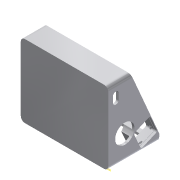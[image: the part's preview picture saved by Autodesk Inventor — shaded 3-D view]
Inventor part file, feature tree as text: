
AUTODESK INVENTOR PART (.ipt)
format: ipt  version: 2019.4 (Build 234330000, 330)  size: 572,928 bytes
history: native  units: mm
features: extrude x14, sketch x14, reference x13, projected_geometry x11, other x7, plane x2, chamfer x1
ambient origin geometry x8: Origin, YZ Plane, XZ Plane, XY Plane, X Axis, Y Axis, Z Axis, Center Point
bodies: Solid1 (feature_tree)
feature tree (62):
  plane  "Work Plane1"
  extrude  "Extrusion1"  Depth=5.0mm
  sketch  "Sketch2"  dims[d3=90.0mm d4=3.0mm d5=0.0mm]
  plane  "Work Plane2"
  extrude  "Extrusion2"  Depth=3.0mm TaperAngle=0.0deg
  extrude  "Extrusion3"  Depth=3.0mm
  extrude  "Extrusion4"  Depth=3.0mm TaperAngle=0.0deg
  extrude  "Extrusion5"  Depth=3.0mm TaperAngle=0.0deg
  extrude  "Extrusion6"  Depth=3.0mm TaperAngle=0.0deg
  extrude  "Extrusion7"  TaperAngle=0.0deg  [1 undecoded]
  extrude  "Extrusion8"  Depth=10.0mm TaperAngle=0.0deg
  extrude  "Extrusion9"  Depth=2.9mm
  extrude  "Extrusion10"  Depth=2.9mm
  extrude  "Extrusion11"  Depth=20.0mm TaperAngle=0.0deg
  extrude  "Extrusion12"  Depth=20.0mm TaperAngle=0.0deg
  extrude  "Extrusion13"  TaperAngle=90.0deg  [1 undecoded]
  extrude  "Extrusion14"  TaperAngle=180.0deg  [1 undecoded]
  chamfer  "Chamfer1"  Distance=11.0mm
  sketch  "Sketch1"  dims[d1=5.0mm d2=5.0mm]
  reference  "Reference1"
  reference  "Reference2"
  projected_geometry  "Projected Loop1"
  sketch  "Sketch3"  dims[d6=5.0mm d7=3.0mm]
  projected_geometry  "Projected Loop2"
  sketch  "Sketch4"  dims[d8=3.0mm d9=0.0mm d10=3.0mm d11=0.0mm]
  reference  "Reference3"
  sketch  "Sketch5"  dims[d12=3.0mm d13=0.0mm d14=3.0mm d15=0.0mm]
  reference  "Reference4"
  reference  "Reference5"
  reference  "Reference6"
  reference  "Reference7"
  reference  "Reference8"
  sketch  "Sketch6"  dims[d16=0.3mm d17=3.0mm d18=0.0mm]
  reference  "Reference9"
  sketch  "Sketch7"  dims[d19=15.0mm d20=0.0mm d21=0.0mm d22=0.0mm]
  projected_geometry  "Projected Loop3"
  sketch  "Sketch8"  dims[d23=10.0mm d24=0.0mm d25=10.0mm d26=0.0mm]
  projected_geometry  "Projected Loop4"
  reference  "Reference10"
  sketch  "Sketch9"  dims[d27=2.9mm d28=2.9mm]
  projected_geometry  "Projected Loop5"
  reference  "Reference11"
  sketch  "Sketch10"  dims[d29=2.9mm d30=2.9mm]
  projected_geometry  "Projected Loop6"
  sketch  "Sketch11"  dims[d31=20.0mm d32=0.0mm d33=20.0mm d34=0.0mm]
  projected_geometry  "Projected Loop7"
  sketch  "Sketch12"  dims[d35=3.0mm d36=20.0mm d37=0.0mm]
  projected_geometry  "Projected Loop8"
  reference  "Reference12"
  sketch  "Sketch13"  dims[d38=22.0mm d39=90.0deg]
  projected_geometry  "Projected Loop9"
  sketch  "Sketch14"  dims[d40=0.0mm d41=180.0deg d42=11.0mm d43=0.0mm d44=2.0mm d45=2.0mm d46=45.0deg]
  reference  "Reference13"
  projected_geometry  "Projected Loop10"
  projected_geometry  "Projected Loop11"
  other  "Assemlby_OpenOxygen.iam"
  other  "00_Arduino_LCD_I2Cstep:1"
  other  "00_LM286:1"
  other  "01_Connector_T:1"
  other  "00_Batterypack:1"
  other  "02_Connector_S:1"
  other  "00_Oxygen_Oxi:1"
note: 3 required parameter values undecoded (feature->parameter linkage not recoverable at this tier; creation-order binding heuristic only, values carry confidence <= 0.55)
